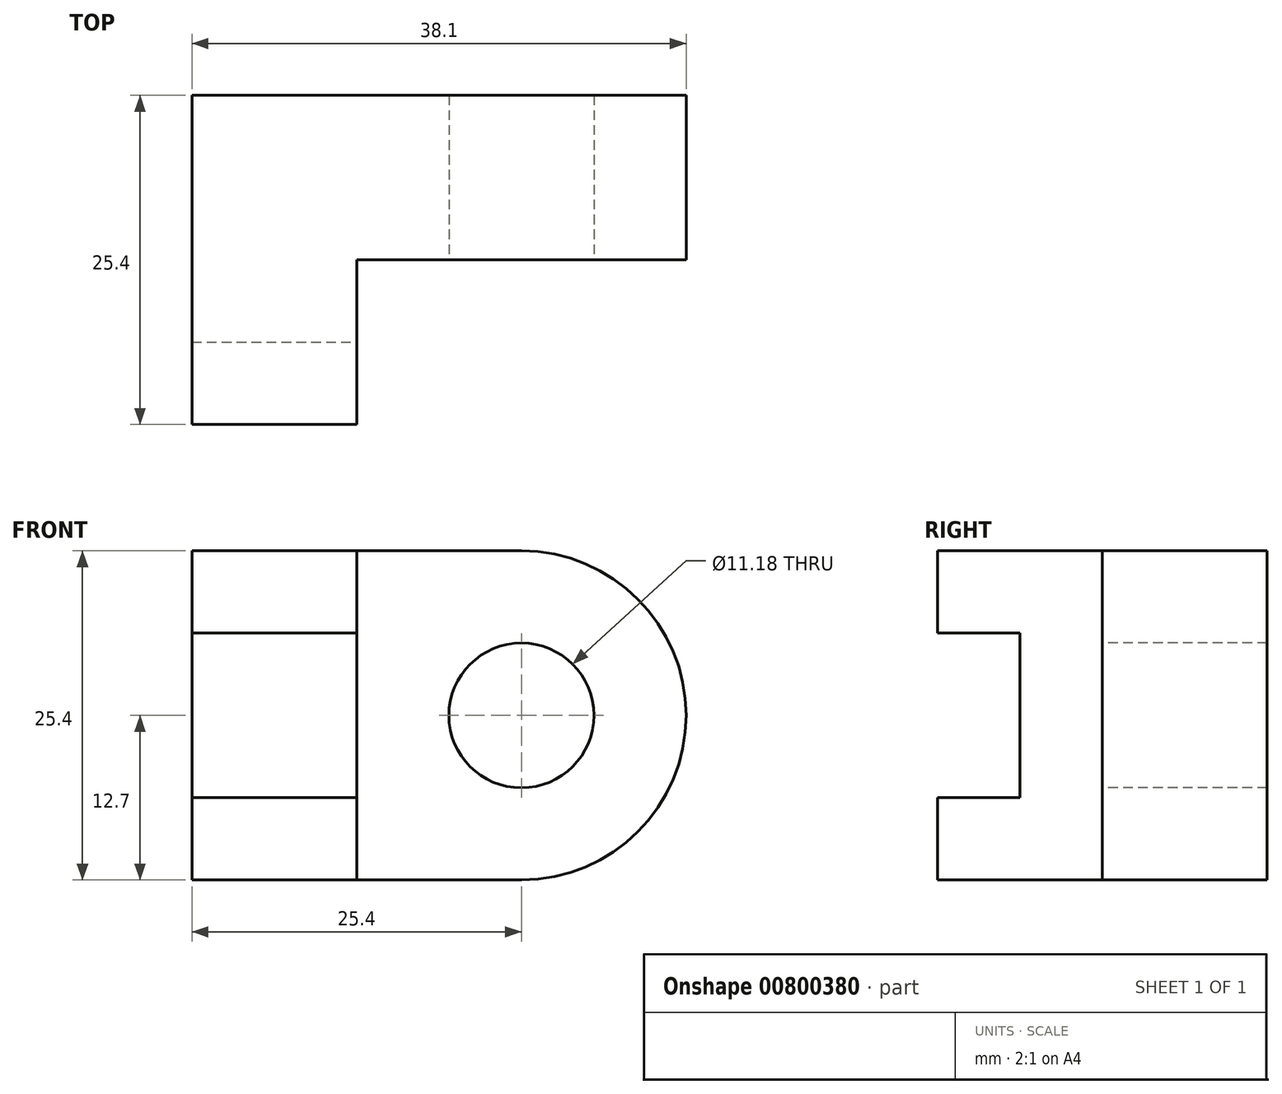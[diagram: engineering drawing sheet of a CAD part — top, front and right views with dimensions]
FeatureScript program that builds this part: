
annotation { "Feature Type Name" : "Feature", "Feature Type Description" : "" }
export const myFeature = defineFeature(function(context is Context, id is Id, definition is map)
    precondition{}
    {
        {
            var Q0;
            Q0=qCreatedBy(makeId("Front.planeOp"),FACE);
            var sketch = newSketch(context, id + "F0", { "sketchPlane" : qUnion([Q0])});
            skLineSegment(sketch, "E0", {"start": v(0, 0) * mm, "end": v(38.1, 0) * mm});
            skLineSegment(sketch, "E1", {"start": v(38.1, 0) * mm, "end": v(38.1, 25.4) * mm});
            skLineSegment(sketch, "E2", {"start": v(38.1, 25.4) * mm, "end": v(0, 25.4) * mm});
            skLineSegment(sketch, "E3", {"start": v(0, 25.4) * mm, "end": v(0, 0) * mm});
            skSolve(sketch);
        }
        {
            var Q0;
            Q0 = qSketchRegion(id + "F0", true);
            extrude(context, id + "F1", {"entities" : qUnion([Q0]), "depth" : 25.4 * mm, "offsetDistance" : 25.4 * mm});
        }
        {
            var Q0;
            Q0=makeQuery(id+"F1.opExtrude","SWEPT_FACE",FACE,{"disambiguationData":[OSD([sQuery(id+"F0.wireOp",EDGE,"E2")])]});
            var sketch = newSketch(context, id + "F2", { "sketchPlane" : qUnion([Q0])});
            skLineSegment(sketch, "E4", {"start": v(0, -25.4) * mm, "end": v(12.7, -25.4) * mm});
            skLineSegment(sketch, "E5", {"start": v(38.1, 0) * mm, "end": v(38.1, -12.7) * mm});
            skLineSegment(sketch, "E6", {"start": v(38.1, -12.7) * mm, "end": v(12.7, -12.7) * mm});
            skLineSegment(sketch, "E7", {"start": v(12.7, -12.7) * mm, "end": v(12.7, -25.4) * mm});
            skSolve(sketch);
        }
        {
            var Q0;
            Q0 = qSketchRegion(id + "F2", true);
            var Q1;
            {var subQ0=sQuery(id+"F2.wireOp",EDGE,"E6");Q1=makeQuery(id+"F2.imprint","IMPRINT",FACE,{"disambiguationData":[TD([[makeQuery(id+"F2.imprint","IMPRINT",EDGE,{"derivedFrom":subQ0}),1.0]])]});}
            extrude(context, id + "F3", {"entities" : qUnion([Q0, Q1]), "operationType" : NewBodyOperationType.REMOVE, "oppositeDirection" : true, "depth" : 25.4 * mm, "offsetDistance" : 25.4 * mm});
        }
        {
            var Q0;
            Q0=makeQuery(id+"F3.boolean.opBoolean","COPY",FACE,{"derivedFrom":makeQuery(id+"F3.opExtrude","SWEPT_FACE",FACE,{"disambiguationData":[OSD([sQuery(id+"F2.wireOp",EDGE,"E7")])]})});
            var sketch = newSketch(context, id + "F4", { "sketchPlane" : qUnion([Q0])});
            skLineSegment(sketch, "E8", {"start": v(-25.4, 25.4) * mm, "end": v(-25.4, 19.05) * mm});
            skLineSegment(sketch, "E9", {"start": v(-25.4, 19.05) * mm, "end": v(-19.05, 19.05) * mm});
            skLineSegment(sketch, "E10", {"start": v(-19.05, 19.05) * mm, "end": v(-19.05, 6.35) * mm});
            skLineSegment(sketch, "E11", {"start": v(-19.05, 6.35) * mm, "end": v(-25.4, 6.35) * mm});
            skLineSegment(sketch, "E12", {"start": v(-25.4, 6.35) * mm, "end": v(-25.4, 0) * mm});
            skSolve(sketch);
        }
        {
            var Q0;
            Q0 = qSketchRegion(id + "F4", true);
            var Q1;
            {var subQ0=sQuery(id+"F4.wireOp",EDGE,"E9");Q1=makeQuery(id+"F4.imprint","IMPRINT",FACE,{"disambiguationData":[TD([[makeQuery(id+"F4.imprint","IMPRINT",EDGE,{"derivedFrom":subQ0}),-1.0]])]});}
            extrude(context, id + "F5", {"entities" : qUnion([Q0, Q1]), "operationType" : NewBodyOperationType.REMOVE, "oppositeDirection" : true, "depth" : 25.4 * mm, "offsetDistance" : 25.4 * mm});
        }
        {
            var Q0;
            Q0=makeQuery(id+"F3.boolean.opBoolean","COPY",FACE,{"derivedFrom":makeQuery(id+"F3.opExtrude","SWEPT_FACE",FACE,{"disambiguationData":[OSD([sQuery(id+"F2.wireOp",EDGE,"E6")])]})});
            var sketch = newSketch(context, id + "F6", { "sketchPlane" : qUnion([Q0])});
            skLineSegment(sketch, "E13", {"start": v(12.7, 12.7) * mm, "end": v(38.1, 12.7) * mm, "construction": true});
            skLineSegment(sketch, "E14", {"start": v(25.4, 12.7) * mm, "end": v(25.4, 25.4) * mm, "construction": true});
            skCircle(sketch, "E15", {"center": v(25.4, 12.7) * mm, "radius": 5.59 * mm});
            skSolve(sketch);
        }
        {
            var Q0;
            Q0=makeQuery(id+"F6.imprint","IMPRINT",FACE,{"disambiguationData":[TD([[makeQuery(id+"F6.imprint","IMPRINT",EDGE,{"derivedFrom":sQuery(id+"F6.wireOp",EDGE,"E15")}),1.0]])]});
            extrude(context, id + "F7", {"entities" : qUnion([Q0]), "operationType" : NewBodyOperationType.REMOVE, "oppositeDirection" : true, "depth" : 25.4 * mm, "offsetDistance" : 25.4 * mm});
        }
        {
            var Q0;
            Q0=makeQuery(id+"F3.boolean.opBoolean","COPY",FACE,{"derivedFrom":makeQuery(id+"F3.opExtrude","SWEPT_FACE",FACE,{"disambiguationData":[OSD([sQuery(id+"F2.wireOp",EDGE,"E6")])]})});
            var sketch = newSketch(context, id + "F8", { "sketchPlane" : qUnion([Q0])});
            skLineSegment(sketch, "E16", {"start": v(12.7, 25.4) * mm, "end": v(25.4, 25.4) * mm, "construction": true});
            skLineSegment(sketch, "E17", {"start": v(12.7, 0) * mm, "end": v(25.4, 0) * mm, "construction": true});
            skArc(sketch, "E18", {"start": v(25.4, 0) * mm, "mid": v(38.1, 12.7) * mm, "end": v(25.4, 25.4) * mm});
            skSolve(sketch);
        }
        {
            var Q0;
            Q0 = qSketchRegion(id + "F8", true);
            var Q1;
            {var subQ0=sQuery(id+"F8.wireOp",EDGE,"E18");var subQ1=sQuery(id+"F2.wireOp",EDGE,"E6");var subQ2=makeQuery(id+"F3.boolean.opBoolean","COPY",EDGE,{"derivedFrom":makeQuery(id+"F3.opExtrude","CAP_EDGE",EDGE,{"disambiguationData":[OSD([subQ1])],"isStart":true})});var subQ3=makeQuery(id+"F8.imprint","INTERSECT",VERTEX,{"derivedFrom":[subQ2,subQ0]});Q1=makeQuery(id+"F8.imprint","IMPRINT",FACE,{"disambiguationData":[TD([[makeQuery(id+"F8.imprint","IMPRINT",EDGE,{"disambiguationData":[TD([[subQ3,1.0]])],"derivedFrom":subQ0}),-1.0]])]});}
            var Q2;
            {var subQ0=sQuery(id+"F8.wireOp",EDGE,"E18");var subQ1=sQuery(id+"F2.wireOp",EDGE,"E6");var subQ2=makeQuery(id+"F3.boolean.opBoolean","COPY",EDGE,{"derivedFrom":makeQuery(id+"F3.opExtrude","CAP_EDGE",EDGE,{"disambiguationData":[OSD([subQ1])],"isStart":false})});var subQ3=makeQuery(id+"F8.imprint","INTERSECT",VERTEX,{"derivedFrom":[subQ2,subQ0]});Q2=makeQuery(id+"F8.imprint","IMPRINT",FACE,{"disambiguationData":[TD([[makeQuery(id+"F8.imprint","IMPRINT",EDGE,{"disambiguationData":[TD([[subQ3,-1.0]])],"derivedFrom":subQ0}),-1.0]])]});}
            extrude(context, id + "F9", {"entities" : qUnion([Q0, Q1, Q2]), "operationType" : NewBodyOperationType.REMOVE, "oppositeDirection" : true, "depth" : 25.4 * mm, "offsetDistance" : 25.4 * mm});
        }
    });
